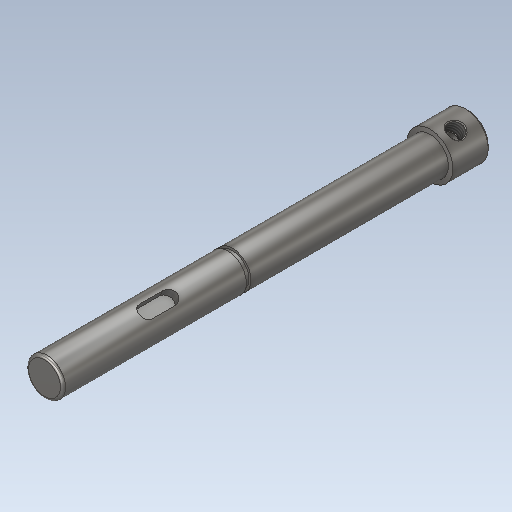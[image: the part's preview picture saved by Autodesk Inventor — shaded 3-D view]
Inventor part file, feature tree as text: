
AUTODESK INVENTOR PART (.ipt)
format: ipt  version: 2020.1 (Build 241239000, 239)  size: 199,680 bytes
history: native  units: mm
features: plane x2, sketch x2, extrude x1, revolve x1, thread x1, fillet x1, chamfer x1, other x1
ambient origin geometry x8: Origin, YZ Plane, XZ Plane, XY Plane, X Axis, Y Axis, Z Axis, Center Point
bodies: Solid1 (feature_tree), Body1 (feature_tree)
feature tree (10):
  plane  "Work Plane1"
  extrude  "Extrusion1"  Depth=2.788mm
  plane  "Work Plane2"
  revolve  "Revolution1"  [1 undecoded]
  thread  "Thread1"  [1 undecoded]
  fillet  "Fillet1"  [1 undecoded]
  chamfer  "Chamfer1"  Angle=90.0deg  [1 undecoded]
  sketch  "Sketch1"  dims[d0=2.0mm d1=2.788mm]
  other  "Work Axis1"
  sketch  "Sketch2"  dims[d2=3.3mm d3=3.0mm d4=0.0mm d5=90.0deg d6=30.0deg d7=90.0deg d8=10.0mm d9=0.0mm d10=0.2mm d11=0.2mm d12=2.0mm d13=45.0deg]
note: 4 required parameter values undecoded (feature->parameter linkage not recoverable at this tier; creation-order binding heuristic only, values carry confidence <= 0.55)